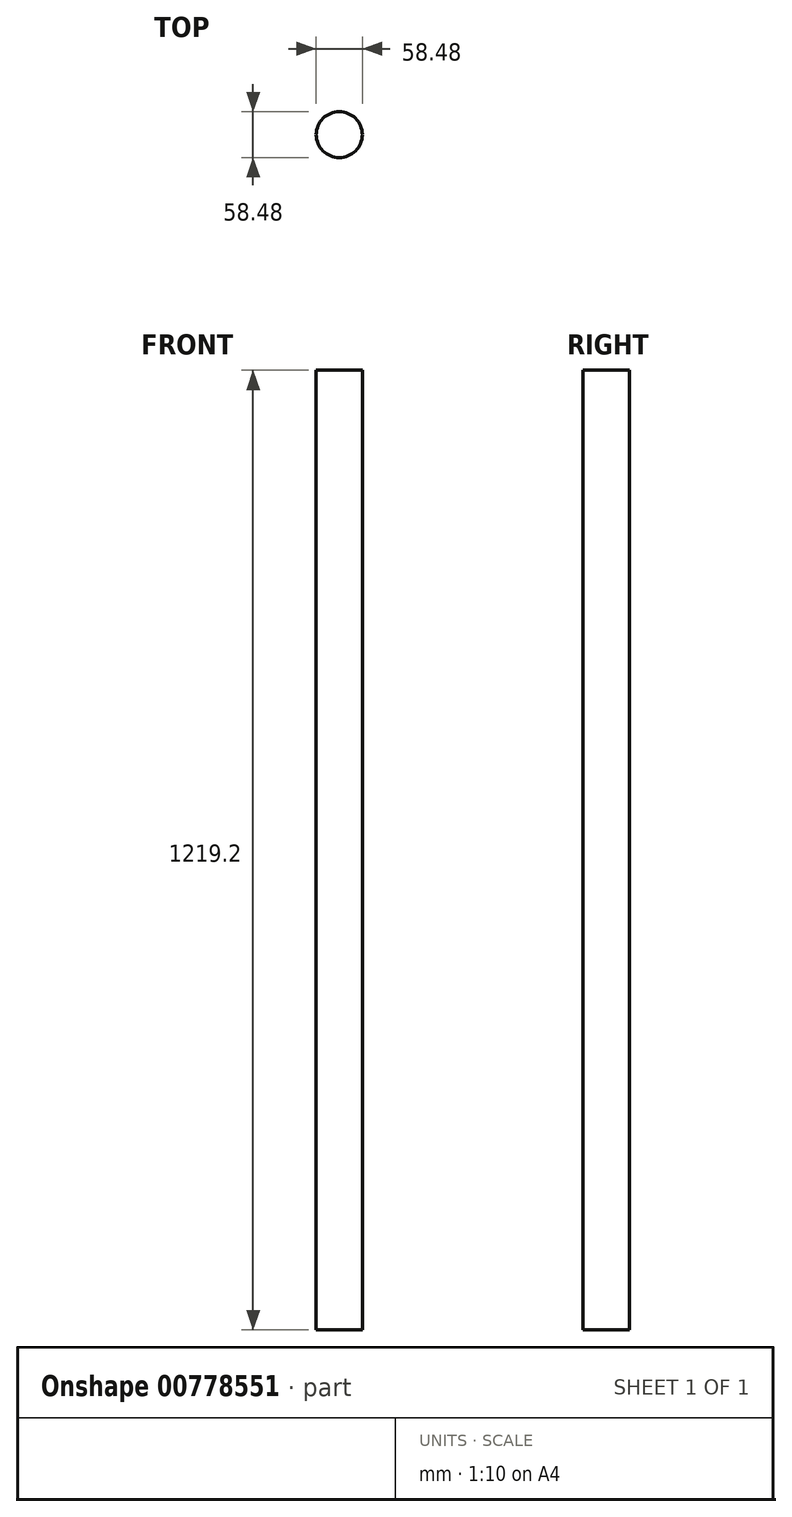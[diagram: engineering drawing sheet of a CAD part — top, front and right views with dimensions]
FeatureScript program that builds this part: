
annotation { "Feature Type Name" : "Feature", "Feature Type Description" : "" }
export const myFeature = defineFeature(function(context is Context, id is Id, definition is map)
    precondition{}
    {
        {
            var Q0;
            Q0=qCreatedBy(makeId("Top.planeOp"),FACE);
            var sketch = newSketch(context, id + "F0", { "sketchPlane" : qUnion([Q0])});
            skCircle(sketch, "E0", {"center": v(0, 0) * mm, "radius": 29.24 * mm});
            skSolve(sketch);
        }
        {
            var Q0;
            Q0=sQuery(id+"F0.wireOp",EDGE,"E0");
            extrude(context, id + "F1", {"bodyType" : ToolBodyType.SURFACE, "surfaceEntities" : qUnion([Q0]), "depth" : 1219.2 * mm, "offsetDistance" : 25.4 * mm});
        }
    });
